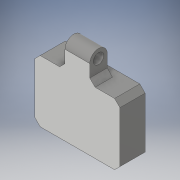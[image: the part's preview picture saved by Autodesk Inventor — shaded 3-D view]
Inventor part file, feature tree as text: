
AUTODESK INVENTOR PART (.ipt)
format: ipt  version: 2018 (Build 220112000, 112)  size: 326,656 bytes
history: native  units: in
note: dims shown in document units (in); Inventor stores cm internally (conversion verified against a paired STEP export)
features: extrude x3, sketch x3, fillet x1, chamfer x1
ambient origin geometry x8: Origin, YZ Plane, XZ Plane, XY Plane, X Axis, Y Axis, Z Axis, Center Point
bodies: Solid1 (feature_tree)
feature tree (8):
  extrude  "Extrusion1"  Depth=0.375in
  extrude  "Extrusion2"  Depth=0.425in
  fillet  "Fillet1"  Radius=0.246in
  chamfer  "Chamfer1"  Distance=0.123in
  extrude  "Extrusion3"  Depth=0.246in TaperAngle=0.0deg
  sketch  "Sketch1"  dims[d0=0.425in d1=0.375in]
  sketch  "Sketch2"  dims[d2=0.35in d3=0.425in d5=0.246in d6=0.0in]
  sketch  "Sketch4"  dims[d7=0.146in d8=0.123in d9=0.246in d10=0.0in d11=0.123in d12=0.075in d13=0.125in d14=45.0deg d17=1.246in d18=0.05in d19=0.125in d22=0.11in d23=0.0in]
